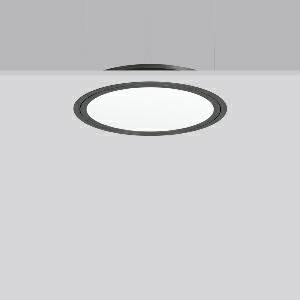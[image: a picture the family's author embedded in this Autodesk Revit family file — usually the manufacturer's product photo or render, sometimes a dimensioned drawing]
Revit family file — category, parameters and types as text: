
# Revit family: triona_round_e_312419_0031_1_12_41f0
name_source: partatom
category: Lighting Fixtures
units: mm (PartAtom-declared; Revit-internal decimal feet)

## family parameters
Cut with Voids When Loaded = No
Host = Face
Light Source = No
Part Type = Normal
Room Calculation Point = No
Round Connector Dimension = Use Diameter
Shared = No

## types (1)
- TRIONA round E (1 x LED Modul 840, 4900 lm, 4000)
    Apparent Load = 48 VA
    CIE Flux Codes = 49 80 96 100 100
    Color Rendering = 80
    Color Temperature = 4000
    Default Elevation = 1800 mm
    Description = Series: TRIONA round
Decorative round LED recessed surface luminaire. Cover made of sheet steel, powder-coated. Frame made of aluminium, powder-coated. Recessed ring: aluminium extrusion profile, powder coated. Light emission through a diffuser: plastic, opal. Lightguide and diffuser made of non-yellowing plastic (PMMA). Lateral light emission (RZB SIDELITE technology) for above-average homogeneous light distribution. Suitable for installation in cavity ceilings. Tool-free mounting system thanks to the rocker arm mechanism (patent pending). Electronic ballast included. Very easy installation thanks to Plug+Play connection. 
Colour: anthracite metallic (DB703)
Diameter: 505 mm
Height: 2 mm
Cut-out diameter: 482 mm
Recess height: 100 mm
Luminaire: recess height: 89 mm
Lamp: LED
Socket: without socket
Colour temperature: 4000K
Colour rendering index (CRI): 80
System power: 48 W
Rated luminous flux: 4900 lm
Luminous efficiency: 102 lm/W
Control gear: Converter, dimmable, DALI
Protection class: I
Type of protection: IP 40
    Height = 0 mm  [stored 0 ft]
    Lamp = 1 x LED Modul 840
    Lamp Light Flux = 4900 lm
    Lamp count = 1
    Length = 505 mm
    Lifetime = 50000 h
    Luminous efficacy = 102 lm/W
    Manufacturer = RZB
    ModVariant = No
    Model = 312419.0031.1.12
    Mounting Place = Ceiling
    Mounting Type = Recessed
    Number of Poles = 1
    OnlyDefault = Yes
    Power Factor = 1
    Product Name = TRIONA round E
    Product group = Recessed modular luminaires
    ProductGroupID = 406
    Protection Class = Protection class I
    Protection Degree = IP 20
    RLX_Detail_Level = 1
    RLX_Emergency_Light_Flux = 0 lm
    RLX_Emergency_Type = 0
    RLX_Emergency_Type_DB = No
    RlxData = <blob elided: 33457 chars, md5=9b3f6ab6>
    Socket = socket
    Standby Power = 0 W
    System Light Flux = 4900 lm
    System Power = 48 W
    Type Comments = Product without accessories
    Type Image = 312419.0031.12.jpg
    URL = http://relux.com
    VarID = ---
    Voltage = 230 V
    Voltage Range = 220-240 V
    Weight = 0.00 kg
    Width = 0 mm  [stored 0 ft]

note: [stored X ft] marks values corroborated as IEEE doubles in the binary element streams (Revit-internal decimal feet)

## geometry (parser evidence)
native form markers: Blend x4, Sweep x10
no freeform markers — native parametric forms only
